# Revit family: CAME_Турникет_Скоростной_SWINGGATE_SWG90MРаздвижнойЦентральныйМодуль
name_source: partatom
category: Специальное оборудование
units: mm (PartAtom-declared; Revit-internal decimal feet)

## family parameters
Всегда вертикально = Да
На основе рабочей плоскости = Нет
Общий = Нет
При загрузке вырезать с полостями = Нет
Размер круглого соединителя = Использовать диаметр
Тип детали = Нормальный
Точка расчета площади = Нет

## types (2) — shared parameters
ADSK_URL документации изделия = https://camerussia.com
ADSK_URL страницы изделия = https://camerussia.com
ADSK_Версия Revit = 2019
ADSK_Версия семейства = 1.0
ADSK_Группирование = SWING GATE
ADSK_Единица измерения = шт.
ADSK_Завод-изготовитель = CAME
ADSK_Классификация нагрузок = Прочее
ADSK_Код изделия = Код КСР 26.30.50.119.61.2.07.09
ADSK_Количество = 1
ADSK_Количество фаз = 1
ADSK_Коэффициент мощности = 0.96
ADSK_Напряжение = 230 В
ADSK_Номинальная мощность = 78 Вт
ADSK_Обозначение = ТУ 26.30.50-001-89603926-2021
ADSK_Полная мощность = 81 В·А
ADSK_Размер_Высота = 1000 мм
ADSK_Размер_Глубина = 1488 мм
BL_BIM library = https://bimlib.pro
CAME_Время открывания (с) = 2.2
CAME_Диапазон рабочих температур (°C) = -20 ÷ +68
CAME_Интенсивность использования (%) = ИНТЕНСИВНОЕ
CAME_Класс защиты (IP) = 44
CAME_Максимальное количество проходов в минуту = 30
CAME_Напряжение электропитания двигателя (В) = 24 В
CAME_Тип механизма турникета = моторизованный
URL = https://camerussia.com
Группа модели = Турникеты
Изготовитель = CAME
Правая = 425 мм
х1 = 73 мм
х2 = 103 мм

## per-type parameters (varying)
| type | ADSK_Марка | ADSK_Масса | ADSK_Масса_Текст | ADSK_Наименование | ADSK_Наименование краткое | ADSK_Размер_Ширина | Левая | Описание |
| 550 + 900 | АРТ:001SWG5590MC | 77 | 77 | Центральный модуль скоростного распашного турникета SWING GATE SWG90 комбинированный, ширина прохода 550 + 900 мм | Центр. модуль турникета SWING GATE SWG90, 550 + 900 мм | 880 мм | 250 мм | Комбинированный центральный модуль распашного турникета SWING GATE SWG90M, оснащенный платой управления и светодиодными указателями прохода и направления. Корпус - нержавеющая сталь. Сервопозиционный электропривод створки с определением препятствий и автоматической разблокировкой при отключении электроэнергии. Створка из 10 мм закаленного стекла. Ширина прохода 550 + 900 мм. Высота створки 1200 мм. Время открытия - 2.2 сек. |
| 900 + 900 | АРТ:001SWG90MC | 90 | 90 | Центральный модуль скоростного распашного турникета SWING GATE SWG90, ширина прохода 900 + 900 мм | Центр. модуль турникета SWING GATE SWG90, 900 + 900 мм | 1055 мм | 425 мм | Центральный модуль распашного турникета SWING GATE SWG90M, оснащенный платой управления и светодиодными указателями прохода и направления. Корпус - нержавеющая сталь. Сервопозиционный электропривод створки с определением препятствий и автоматической разблокировкой при отключении электроэнергии. Створка из 10 мм закаленного стекла. Ширина прохода 900 мм. Высота створки 1200 мм. Время открытия - 2.2 сек. |
